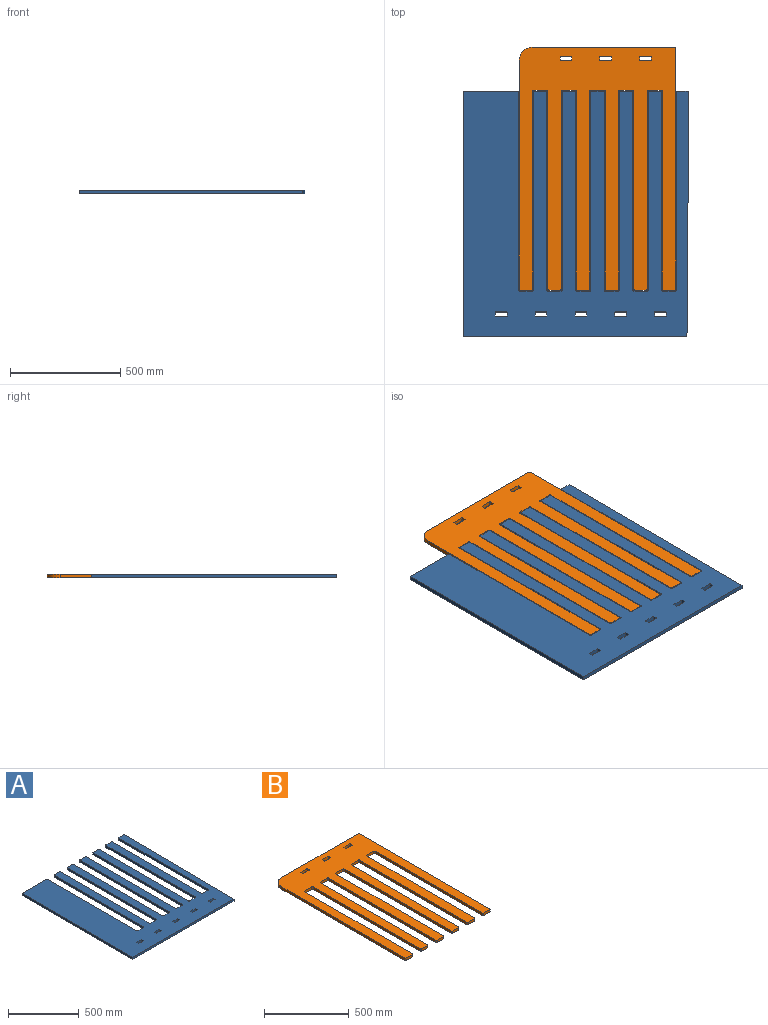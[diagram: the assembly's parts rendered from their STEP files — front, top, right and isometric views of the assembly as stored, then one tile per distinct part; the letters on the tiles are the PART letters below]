
ASSEMBLY  parts=2 mates=1
PART A: 95 faces, bbox 1022x1112.5x18 mm
  f0: plane 1112.5x1022.04mm, normal (0,0,1), area 752829.8mm2, adj f2,f3,f4,f5,f6,f7,f8,f9
  f1: plane 1112.5x1022.04mm, normal (0,0,-1), area 752829.8mm2, adj f2,f3,f4,f5,f6,f7,f8,f9
  f2: plane 46.7x18mm, normal (0,1,0), area 840.7mm2, adj f0,f1,f3,f91
  f3: cylinder r=5mm len=18mm, axis (0,0,-1), area 141.4mm2, adj f0,f1,f2,f4
  f4: plane 895.74x18mm, normal (-1,0,0), area 16123.4mm2, adj f0,f1,f3,f5
  f5: cylinder r=5mm len=18mm, axis (0,0,-1), area 141.4mm2, adj f0,f1,f4,f6
  f6: plane 58.8x18mm, normal (0,1,0), area 1058.4mm2, adj f0,f1,f5,f7
  f7: cylinder r=5mm len=18mm, axis (0,0,-1), area 141.4mm2, adj f0,f1,f6,f8
  f8: plane 895.74x18mm, normal (1,0,0), area 16123.4mm2, adj f0,f1,f7,f9
  f9: cylinder r=5mm len=18mm, axis (0,0,-1), area 141.4mm2, adj f0,f1,f8,f10
  f10: plane 50.8x18mm, normal (0,1,0), area 914.4mm2, adj f0,f1,f9,f11
  f11: cylinder r=5mm len=18mm, axis (0,0,-1), area 141.4mm2, adj f0,f1,f10,f12
  f12: plane 895.74x18mm, normal (-1,0,0), area 16123.4mm2, adj f0,f1,f11,f13
  f13: cylinder r=5mm len=18mm, axis (0,0,-1), area 141.4mm2, adj f0,f1,f12,f14
  f14: plane 58.8x18mm, normal (0,1,0), area 1058.4mm2, adj f0,f1,f13,f15
  f15: cylinder r=5mm len=18mm, axis (0,0,-1), area 141.4mm2, adj f0,f1,f14,f16
  f16: plane 895.74x18mm, normal (1,0,0), area 16123.4mm2, adj f0,f1,f15,f17
  f17: cylinder r=5mm len=18mm, axis (0,0,-1), area 141.4mm2, adj f0,f1,f16,f18
  f18: plane 50.8x18mm, normal (0,1,0), area 914.4mm2, adj f0,f1,f17,f19
  f19: cylinder r=5mm len=18mm, axis (0,0,-1), area 141.4mm2, adj f0,f1,f18,f20
  f20: plane 895.74x18mm, normal (-1,0,0), area 16123.4mm2, adj f0,f1,f19,f21
  f21: cylinder r=5mm len=18mm, axis (0,0,-1), area 141.4mm2, adj f0,f1,f20,f22
  f22: plane 58.8x18mm, normal (0,1,0), area 1058.4mm2, adj f0,f1,f21,f23
  f23: cylinder r=5mm len=18mm, axis (0,0,-1), area 141.4mm2, adj f0,f1,f22,f24
  f24: plane 895.74x18mm, normal (1,0,0), area 16123.4mm2, adj f0,f1,f23,f25
  f25: cylinder r=5mm len=18mm, axis (0,0,-1), area 141.4mm2, adj f0,f1,f24,f26
  f26: plane 50.8x18mm, normal (0,1,0), area 914.4mm2, adj f0,f1,f25,f27
  f27: cylinder r=5mm len=18mm, axis (0,0,-1), area 141.4mm2, adj f0,f1,f26,f28
  f28: plane 895.74x18mm, normal (-1,0,0), area 16123.4mm2, adj f0,f1,f27,f29
  f29: cylinder r=5mm len=18mm, axis (0,0,-1), area 141.4mm2, adj f0,f1,f28,f30
  f30: plane 58.8x18mm, normal (0,1,0), area 1058.4mm2, adj f0,f1,f29,f31
  f31: cylinder r=5mm len=18mm, axis (0,0,-1), area 141.4mm2, adj f0,f1,f30,f32
  f32: plane 895.74x18mm, normal (1,0,0), area 16123.4mm2, adj f0,f1,f31,f33
  f33: cylinder r=5mm len=18mm, axis (0,0,-1), area 141.4mm2, adj f0,f1,f32,f34
  f34: plane 50.8x18mm, normal (0,1,0), area 914.4mm2, adj f0,f1,f33,f35
  f35: cylinder r=5mm len=18mm, axis (0,0,-1), area 141.4mm2, adj f0,f1,f34,f36
  f36: plane 895.74x18mm, normal (-1,0,0), area 16123.4mm2, adj f0,f1,f35,f37
  f37: cylinder r=5mm len=18mm, axis (0,0,-1), area 141.4mm2, adj f0,f1,f36,f38
  f38: plane 58.8x18mm, normal (0,1,0), area 1058.4mm2, adj f0,f1,f37,f39
  f39: cylinder r=5mm len=18mm, axis (0,0,-1), area 141.4mm2, adj f0,f1,f38,f40
  f40: plane 895.74x18mm, normal (1,0,0), area 16123.4mm2, adj f0,f1,f39,f41
  f41: cylinder r=5mm len=18mm, axis (0,0,-1), area 141.4mm2, adj f0,f1,f40,f42
  f42: plane 50.8x18mm, normal (0,1,0), area 914.4mm2, adj f0,f1,f41,f92
  f43: plane 895.74x18mm, normal (-1,0,0), area 16123.4mm2, adj f0,f1,f44,f92
  f44: cylinder r=5mm len=18mm, axis (0,0,-1), area 141.4mm2, adj f0,f1,f43,f45
  f45: plane 58.8x18mm, normal (0,1,0), area 1058.4mm2, adj f0,f1,f44,f46
  f46: cylinder r=5mm len=18mm, axis (0,0,-1), area 141.4mm2, adj f0,f1,f45,f47
  f47: plane 895.74x18mm, normal (1,0,0), area 16123.4mm2, adj f0,f1,f46,f48
  f48: cylinder r=5mm len=18mm, axis (0,0,-1), area 141.4mm2, adj f0,f1,f47,f49
  f49: plane 245x18mm, normal (0,1,0), area 4410mm2, adj f0,f1,f48,f93
  f50: plane 1013.5x18mm, normal (0,-1,0), area 18243.1mm2, adj f0,f1,f93,f94
  f51: plane 18x18mm, normal (1,0,0), area 324mm2, adj f0,f1,f83,f86
  f52: plane 50x18mm, normal (0,1,0), area 900mm2, adj f0,f1,f83,f84
  f53: plane 18x18mm, normal (-1,0,0), area 324mm2, adj f0,f1,f84,f85
  f54: plane 50x18mm, normal (0,-1,0), area 900mm2, adj f0,f1,f85,f86
  f55: plane 18x18mm, normal (1,0,0), area 324mm2, adj f0,f1,f79,f82
  f56: plane 50x18mm, normal (0,1,0), area 900mm2, adj f0,f1,f81,f82
  f57: plane 18x18mm, normal (-1,0,0), area 324mm2, adj f0,f1,f80,f81
  f58: plane 50x18mm, normal (0,-1,0), area 900mm2, adj f0,f1,f79,f80
  f59: plane 18x18mm, normal (1,0,0), area 324mm2, adj f0,f1,f75,f78
  f60: plane 50x18mm, normal (0,1,0), area 900mm2, adj f0,f1,f77,f78
  f61: plane 18x18mm, normal (-1,0,0), area 324mm2, adj f0,f1,f76,f77
  f62: plane 50x18mm, normal (0,-1,0), area 900mm2, adj f0,f1,f75,f76
  f63: plane 18x18mm, normal (-1,0,0), area 324mm2, adj f0,f1,f71,f74
  f64: plane 50x18mm, normal (0,-1,0), area 900mm2, adj f0,f1,f73,f74
  f65: plane 18x18mm, normal (1,0,0), area 324mm2, adj f0,f1,f72,f73
  f66: plane 50x18mm, normal (0,1,0), area 900mm2, adj f0,f1,f71,f72
  f67: plane 18x18mm, normal (1,0,0), area 324mm2, adj f0,f1,f87,f90
  f68: plane 50x18mm, normal (0,1,0), area 900mm2, adj f0,f1,f89,f90
  f69: plane 18x18mm, normal (-1,0,0), area 324mm2, adj f0,f1,f88,f89
  f70: plane 50x18mm, normal (0,-1,0), area 900mm2, adj f0,f1,f87,f88
  f71: cylinder r=1.5mm len=18mm, axis (0,0,1), area 42.4mm2, adj f0,f1,f63,f66
  f72: cylinder r=1.5mm len=18mm, axis (0,0,-1), area 42.4mm2, adj f0,f1,f65,f66
  f73: cylinder r=1.5mm len=18mm, axis (0,0,1), area 42.4mm2, adj f0,f1,f64,f65
  f74: cylinder r=1.5mm len=18mm, axis (0,0,-1), area 42.4mm2, adj f0,f1,f63,f64
  f75: cylinder r=1.5mm len=18mm, axis (0,0,1), area 42.4mm2, adj f0,f1,f59,f62
  f76: cylinder r=1.5mm len=18mm, axis (0,0,-1), area 42.4mm2, adj f0,f1,f61,f62
  f77: cylinder r=1.5mm len=18mm, axis (0,0,1), area 42.4mm2, adj f0,f1,f60,f61
  f78: cylinder r=1.5mm len=18mm, axis (0,0,-1), area 42.4mm2, adj f0,f1,f59,f60
  f79: cylinder r=1.5mm len=18mm, axis (0,0,1), area 42.4mm2, adj f0,f1,f55,f58
  f80: cylinder r=1.5mm len=18mm, axis (0,0,-1), area 42.4mm2, adj f0,f1,f57,f58
  f81: cylinder r=1.5mm len=18mm, axis (0,0,1), area 42.4mm2, adj f0,f1,f56,f57
  f82: cylinder r=1.5mm len=18mm, axis (0,0,-1), area 42.4mm2, adj f0,f1,f55,f56
  f83: cylinder r=1.5mm len=18mm, axis (0,0,-1), area 42.4mm2, adj f0,f1,f51,f52
  f84: cylinder r=1.5mm len=18mm, axis (0,0,1), area 42.4mm2, adj f0,f1,f52,f53
  f85: cylinder r=1.5mm len=18mm, axis (0,0,-1), area 42.4mm2, adj f0,f1,f53,f54
  f86: cylinder r=1.5mm len=18mm, axis (0,0,1), area 42.4mm2, adj f0,f1,f51,f54
  f87: cylinder r=1.5mm len=18mm, axis (0,0,1), area 42.4mm2, adj f0,f1,f67,f70
  f88: cylinder r=1.5mm len=18mm, axis (0,0,-1), area 42.4mm2, adj f0,f1,f69,f70
  f89: cylinder r=1.5mm len=18mm, axis (0,0,1), area 42.4mm2, adj f0,f1,f68,f69
  f90: cylinder r=1.5mm len=18mm, axis (0,0,-1), area 42.4mm2, adj f0,f1,f67,f68
  f91: cylinder r=5mm len=18mm, axis (0,0,1), area 70.7mm2, adj f0,f1,f2,f94
  f92: cylinder r=5mm len=18mm, axis (0,0,-1), area 141.4mm2, adj f0,f1,f42,f43
  f93: plane 1112.5x18mm, normal (-1,0,0), area 20025mm2, adj f0,f1,f49,f50
  f94: plane 1111.04x18mm, normal (1,-0.01,0), area 19999.2mm2, adj f0,f1,f50,f91
PART B: 74 faces, bbox 708.8x1100x18 mm
  f0: plane 1100x708.8mm, normal (0,0,1), area 463810.5mm2, adj f2,f3,f4,f5,f6,f7,f8,f9
  f1: plane 1100x708.8mm, normal (0,0,-1), area 463810.5mm2, adj f2,f3,f4,f5,f6,f7,f8,f9
  f2: plane 896.24x18mm, normal (-1,0,0), area 16132.4mm2, adj f0,f1,f26,f48
  f3: plane 50.8x18mm, normal (0,-1,0), area 914.4mm2, adj f0,f1,f26,f27
  f4: plane 1090x18mm, normal (1,0,0), area 19620mm2, adj f0,f1,f27,f28
  f5: plane 643.8x18mm, normal (0,1,0), area 11588.4mm2, adj f0,f1,f28,f49
  f6: plane 1035x18mm, normal (-1,0,0), area 18630mm2, adj f0,f1,f29,f49
  f7: plane 50.8x18mm, normal (0,-1,0), area 914.4mm2, adj f0,f1,f29,f30
  f8: plane 896.24x18mm, normal (1,0,0), area 16132.4mm2, adj f0,f1,f30,f31
  f9: plane 58.8x18mm, normal (0,-1,0), area 1058.4mm2, adj f0,f1,f31,f32
  f10: plane 896.24x18mm, normal (-1,0,0), area 16132.4mm2, adj f0,f1,f32,f33
  f11: plane 50.8x18mm, normal (0,-1,0), area 914.4mm2, adj f0,f1,f33,f34
  f12: plane 896.24x18mm, normal (1,0,0), area 16132.4mm2, adj f0,f1,f34,f35
  f13: plane 58.8x18mm, normal (0,-1,0), area 1058.4mm2, adj f0,f1,f35,f36
  f14: plane 896.24x18mm, normal (-1,0,0), area 16132.4mm2, adj f0,f1,f36,f37
  f15: plane 50.8x18mm, normal (0,-1,0), area 914.4mm2, adj f0,f1,f37,f38
  f16: plane 896.24x18mm, normal (1,0,0), area 16132.4mm2, adj f0,f1,f38,f39
  f17: plane 58.8x18mm, normal (0,-1,0), area 1058.4mm2, adj f0,f1,f39,f40
  f18: plane 896.24x18mm, normal (-1,0,0), area 16132.4mm2, adj f0,f1,f40,f41
  f19: plane 50.8x18mm, normal (0,-1,0), area 914.4mm2, adj f0,f1,f41,f42
  f20: plane 896.24x18mm, normal (1,0,0), area 16132.4mm2, adj f0,f1,f42,f43
  f21: plane 58.8x18mm, normal (0,-1,0), area 1058.4mm2, adj f0,f1,f43,f44
  f22: plane 896.24x18mm, normal (-1,0,0), area 16132.4mm2, adj f0,f1,f44,f45
  f23: plane 50.8x18mm, normal (0,-1,0), area 914.4mm2, adj f0,f1,f45,f46
  f24: plane 896.24x18mm, normal (1,0,0), area 16132.4mm2, adj f0,f1,f46,f47
  f25: plane 58.8x18mm, normal (0,-1,0), area 1058.4mm2, adj f0,f1,f47,f48
  f26: cylinder r=5mm len=18mm, axis (0,0,1), area 141.4mm2, adj f0,f1,f2,f3
  f27: cylinder r=5mm len=18mm, axis (0,0,1), area 141.4mm2, adj f0,f1,f3,f4
  f28: cylinder r=5mm len=18mm, axis (0,0,-1), area 141.4mm2, adj f0,f1,f4,f5
  f29: cylinder r=5mm len=18mm, axis (0,0,-1), area 141.4mm2, adj f0,f1,f6,f7
  f30: cylinder r=5mm len=18mm, axis (0,0,-1), area 141.4mm2, adj f0,f1,f7,f8
  f31: cylinder r=5mm len=18mm, axis (0,0,1), area 141.4mm2, adj f0,f1,f8,f9
  f32: cylinder r=5mm len=18mm, axis (0,0,-1), area 141.4mm2, adj f0,f1,f9,f10
  f33: cylinder r=5mm len=18mm, axis (0,0,1), area 141.4mm2, adj f0,f1,f10,f11
  f34: cylinder r=5mm len=18mm, axis (0,0,-1), area 141.4mm2, adj f0,f1,f11,f12
  f35: cylinder r=5mm len=18mm, axis (0,0,1), area 141.4mm2, adj f0,f1,f12,f13
  f36: cylinder r=5mm len=18mm, axis (0,0,-1), area 141.4mm2, adj f0,f1,f13,f14
  f37: cylinder r=5mm len=18mm, axis (0,0,1), area 141.4mm2, adj f0,f1,f14,f15
  f38: cylinder r=5mm len=18mm, axis (0,0,-1), area 141.4mm2, adj f0,f1,f15,f16
  f39: cylinder r=5mm len=18mm, axis (0,0,1), area 141.4mm2, adj f0,f1,f16,f17
  f40: cylinder r=5mm len=18mm, axis (0,0,-1), area 141.4mm2, adj f0,f1,f17,f18
  f41: cylinder r=5mm len=18mm, axis (0,0,1), area 141.4mm2, adj f0,f1,f18,f19
  f42: cylinder r=5mm len=18mm, axis (0,0,-1), area 141.4mm2, adj f0,f1,f19,f20
  f43: cylinder r=5mm len=18mm, axis (0,0,1), area 141.4mm2, adj f0,f1,f20,f21
  f44: cylinder r=5mm len=18mm, axis (0,0,-1), area 141.4mm2, adj f0,f1,f21,f22
  f45: cylinder r=5mm len=18mm, axis (0,0,1), area 141.4mm2, adj f0,f1,f22,f23
  f46: cylinder r=5mm len=18mm, axis (0,0,-1), area 141.4mm2, adj f0,f1,f23,f24
  f47: cylinder r=5mm len=18mm, axis (0,0,1), area 141.4mm2, adj f0,f1,f24,f25
  f48: cylinder r=5mm len=18mm, axis (0,0,-1), area 141.4mm2, adj f0,f1,f2,f25
  f49: cylinder r=60mm len=60mm, axis (0,0,1), area 1696.5mm2, adj f0,f1,f5,f6
  f50: plane 50x18mm, normal (0,-1,0), area 900mm2, adj f0,f1,f62,f65
  f51: plane 18x18mm, normal (1,0,0), area 324mm2, adj f0,f1,f64,f65
  f52: plane 50x18mm, normal (0,1,0), area 900mm2, adj f0,f1,f63,f64
  f53: plane 18x18mm, normal (-1,0,0), area 324mm2, adj f0,f1,f62,f63
  f54: plane 50x18mm, normal (0,-1,0), area 900mm2, adj f0,f1,f66,f69
  f55: plane 18x18mm, normal (1,0,0), area 324mm2, adj f0,f1,f66,f67
  f56: plane 50x18mm, normal (0,1,0), area 900mm2, adj f0,f1,f67,f68
  f57: plane 18x18mm, normal (-1,0,0), area 324mm2, adj f0,f1,f68,f69
  f58: plane 50x18mm, normal (0,1,0), area 900mm2, adj f0,f1,f70,f73
  f59: plane 18x18mm, normal (-1,0,0), area 324mm2, adj f0,f1,f72,f73
  f60: plane 50x18mm, normal (0,-1,0), area 900mm2, adj f0,f1,f71,f72
  f61: plane 18x18mm, normal (1,0,0), area 324mm2, adj f0,f1,f70,f71
  f62: cylinder r=1.5mm len=18mm, axis (0,0,1), area 42.4mm2, adj f0,f1,f50,f53
  f63: cylinder r=1.5mm len=18mm, axis (0,0,-1), area 42.4mm2, adj f0,f1,f52,f53
  f64: cylinder r=1.5mm len=18mm, axis (0,0,1), area 42.4mm2, adj f0,f1,f51,f52
  f65: cylinder r=1.5mm len=18mm, axis (0,0,-1), area 42.4mm2, adj f0,f1,f50,f51
  f66: cylinder r=1.5mm len=18mm, axis (0,0,-1), area 42.4mm2, adj f0,f1,f54,f55
  f67: cylinder r=1.5mm len=18mm, axis (0,0,1), area 42.4mm2, adj f0,f1,f55,f56
  f68: cylinder r=1.5mm len=18mm, axis (0,0,-1), area 42.4mm2, adj f0,f1,f56,f57
  f69: cylinder r=1.5mm len=18mm, axis (0,0,1), area 42.4mm2, adj f0,f1,f54,f57
  f70: cylinder r=1.5mm len=18mm, axis (0,0,1), area 42.4mm2, adj f0,f1,f58,f61
  f71: cylinder r=1.5mm len=18mm, axis (0,0,-1), area 42.4mm2, adj f0,f1,f60,f61
  f72: cylinder r=1.5mm len=18mm, axis (0,0,1), area 42.4mm2, adj f0,f1,f59,f60
  f73: cylinder r=1.5mm len=18mm, axis (0,0,-1), area 42.4mm2, adj f0,f1,f58,f59
PLACE A t=(14.81,113.31,-114.48)mm
PLACE B t=(14.81,115.31,-157.48)mm
MATE fastened B.f0 <-> A.f0  axis (0,0,1) through (-50.5,-416.05,157.52)mm
